# Revit family: QF_Summit_BIM44GIFADA_ADA_Compliant_Ice_Maker
name_source: partatom
category: Specialty Equipment
units: mm (PartAtom-declared; Revit-internal decimal feet)

## family parameters
Always vertical = Yes
Cut with Voids When Loaded = No
Part Type = Normal
Room Calculation Point = No
Round Connector Dimension = Use Diameter
Shared = No
Work Plane-Based = No

## types (1)
- QF_Summit_BIM44GIFADA_ADA_Compliant_Ice_Maker
    Apparent Power = 552 VA
    BTUH = 0.0 Btu/h
    Cold Water Connection Height = 0"
    Cold Water Flow = 0 GPM
    Cold Water Maximum Pressure = 0.00 psi
    Cold Water Minimum Pressure = 0.00 psi
    Cold Water RI Height = 0"
    Cold Water Size = 0"
    Cold Water Temperature Recommended = -460 °F
    Conn Conduit = Yes
    Cycle = 60 Hz
    Default Elevation = 0"
    Depth = 23 1/2"
    Description = ADA Compliant Ice Maker
    Direct Waste Connection Height = 0"
    Direct Waste Flow = 0 GPM
    Direct Waste RI Height = 0"
    Direct Waste Size = 0"
    Elec Conn Connection Height = 0"
    Elec Conn RI Height = 0"
    FL Amps = 5 A
    Foodservice Equipment Identifier = Yes
    Height = 32 3/8"
    Identify Quantity as Lot = Yes
    Indirect Waste Connection Height = 0"
    Indirect Waste Flow = 0 GPM
    Indirect Waste Size = 1"
    Length = 14 1/2"
    Manufacturer = Summit
    Max Overcurrent Protection = 0 A
    Min Ckt Ampacity = 0 A
    Model = BIM44GIFADA
    Number of Poles = 1
    Phase = 1
    Refrigerant Type = R134a
    Refrigerant Volume = 0.00 kip
    Volts = 115 V
    Waste Water Discharge Temperature = -460 °F
    Watts = 552 W
    Weight in Pounds = 100

## geometry (parser evidence)
native form markers: Sweep x2
no freeform markers — native parametric forms only
